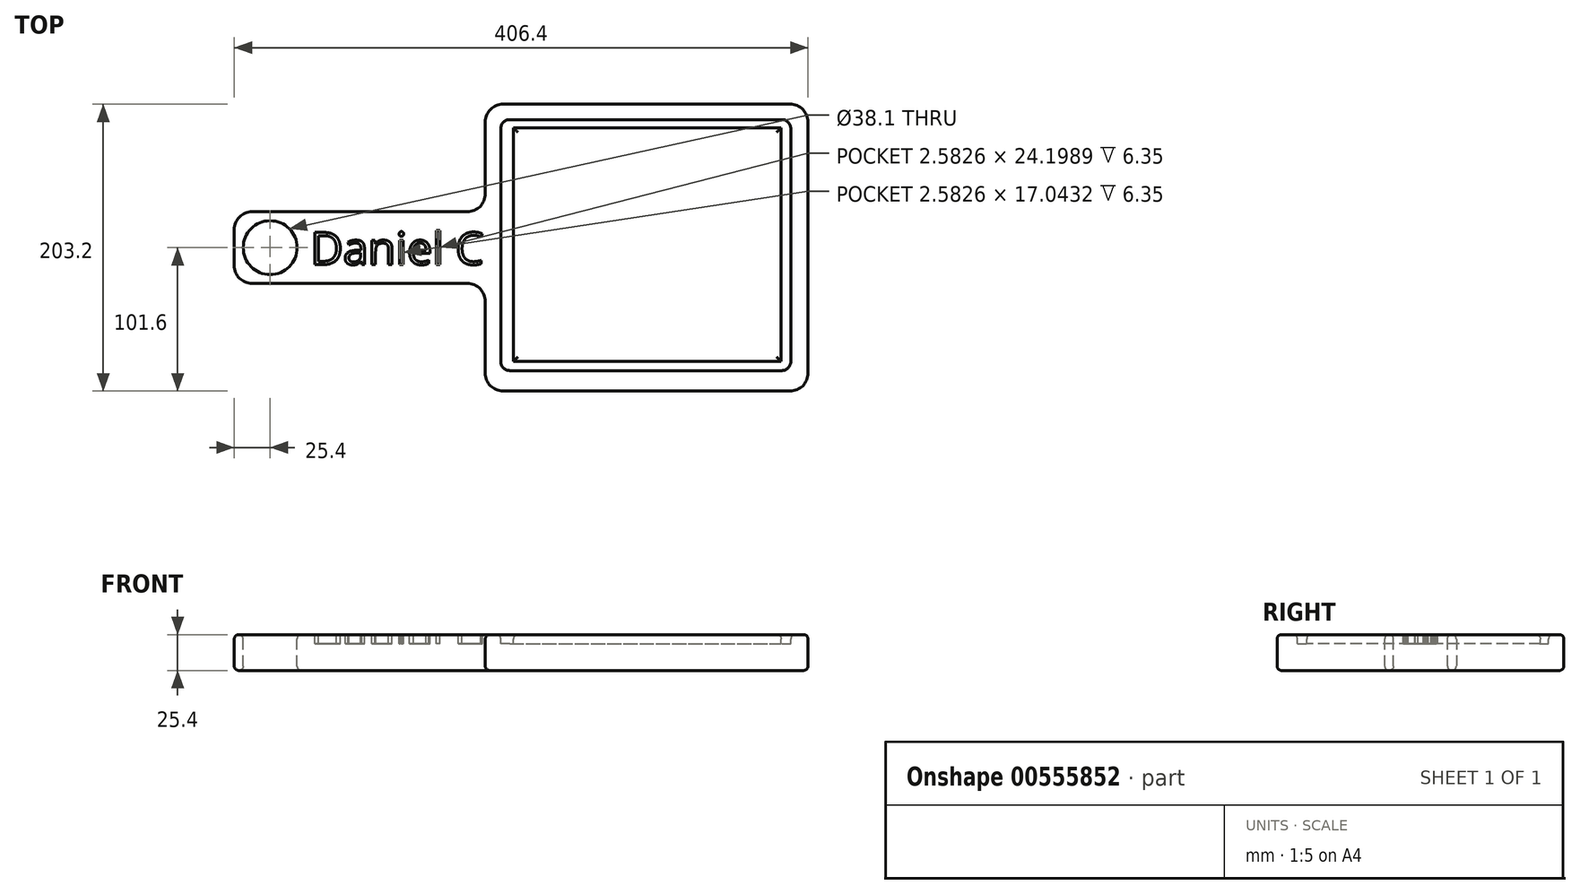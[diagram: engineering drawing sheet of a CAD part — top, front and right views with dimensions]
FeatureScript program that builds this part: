
annotation { "Feature Type Name" : "Feature", "Feature Type Description" : "" }
export const myFeature = defineFeature(function(context is Context, id is Id, definition is map)
    precondition{}
    {
        {
            var Q0;
            Q0=qCreatedBy(makeId("Top.planeOp"),FACE);
            var sketch = newSketch(context, id + "F0", { "sketchPlane" : qUnion([Q0])});
            skLineSegment(sketch, "E0.bottom", {"start": v(0, 0) * mm, "end": v(228.6, 0) * mm});
            skLineSegment(sketch, "E0.top", {"start": v(0, 203.2) * mm, "end": v(228.6, 203.2) * mm});
            skLineSegment(sketch, "E0.left", {"start": v(0, 0) * mm, "end": v(0, 203.2) * mm});
            skLineSegment(sketch, "E0.right", {"start": v(228.6, 0) * mm, "end": v(228.6, 203.2) * mm});
            skLineSegment(sketch, "E1.bottom", {"start": v(0, 127) * mm, "end": v(-177.8, 127) * mm});
            skLineSegment(sketch, "E1.top", {"start": v(0, 76.2) * mm, "end": v(-177.8, 76.2) * mm});
            skLineSegment(sketch, "E1.left", {"start": v(0, 127) * mm, "end": v(0, 76.2) * mm});
            skLineSegment(sketch, "E1.right", {"start": v(-177.8, 127) * mm, "end": v(-177.8, 76.2) * mm});
            skSolve(sketch);
        }
        {
            var Q0;
            Q0=makeQuery(id+"F0.imprint","IMPRINT",FACE,{"disambiguationData":[TD([[makeQuery(id+"F0.imprint","IMPRINT",EDGE,{"derivedFrom":sQuery(id+"F0.wireOp",EDGE,"E1.bottom")}),1.0]])]});
            var Q1;
            {var subQ3=sQuery(id+"F0.wireOp",EDGE,"E0.bottom");Q1=makeQuery(id+"F0.imprint","IMPRINT",FACE,{"disambiguationData":[TD([[makeQuery(id+"F0.imprint","IMPRINT",EDGE,{"derivedFrom":subQ3}),1.0]])]});}
            extrude(context, id + "F1", {"entities" : qUnion([Q0, Q1]), "depth" : 25.4 * mm, "offsetDistance" : 25.4 * mm});
        }
        {
            var Q0;
            Q0=makeQuery(id+"F1.opExtrude","CAP_FACE",FACE,{"disambiguationData":[OSD([sQuery(id+"F0.wireOp",EDGE,"E0.bottom"),sQuery(id+"F0.wireOp",EDGE,"E0.top"),sQuery(id+"F0.wireOp",EDGE,"E0.left"),sQuery(id+"F0.wireOp",EDGE,"E0.right"),sQuery(id+"F0.wireOp",EDGE,"E1.bottom"),sQuery(id+"F0.wireOp",EDGE,"E1.top"),sQuery(id+"F0.wireOp",EDGE,"E1.right")])],"isStart":false});
            var sketch = newSketch(context, id + "F2", { "sketchPlane" : qUnion([Q0])});
            skCircle(sketch, "E2", {"center": v(-152.4, 101.6) * mm, "radius": 19.05 * mm});
            skSolve(sketch);
        }
        {
            var Q0;
            Q0 = qSketchRegion(id + "F2", true);
            extrude(context, id + "F3", {"entities" : qUnion([Q0]), "operationType" : NewBodyOperationType.REMOVE, "oppositeDirection" : true, "depth" : 25.4 * mm, "offsetDistance" : 25.4 * mm});
        }
        {
            var Q0;
            Q0=makeQuery(id+"F1.opExtrude","CAP_FACE",FACE,{"disambiguationData":[OSD([sQuery(id+"F0.wireOp",EDGE,"E0.bottom"),sQuery(id+"F0.wireOp",EDGE,"E0.top"),sQuery(id+"F0.wireOp",EDGE,"E0.left"),sQuery(id+"F0.wireOp",EDGE,"E0.right"),sQuery(id+"F0.wireOp",EDGE,"E1.bottom"),sQuery(id+"F0.wireOp",EDGE,"E1.top"),sQuery(id+"F0.wireOp",EDGE,"E1.right")])],"isStart":false});
            var sketch = newSketch(context, id + "F4", { "sketchPlane" : qUnion([Q0])});
            skLineSegment(sketch, "E3.bottom", {"start": v(11, 192.3) * mm, "end": v(216.38, 192.3) * mm});
            skLineSegment(sketch, "E3.top", {"start": v(11, 14.5) * mm, "end": v(216.38, 14.5) * mm});
            skLineSegment(sketch, "E3.left", {"start": v(11, 192.3) * mm, "end": v(11, 14.5) * mm});
            skLineSegment(sketch, "E3.right", {"start": v(216.38, 192.3) * mm, "end": v(216.38, 14.5) * mm});
            skLineSegment(sketch, "E4.bottom", {"start": v(19.88, 186.5) * mm, "end": v(209.54, 186.5) * mm});
            skLineSegment(sketch, "E4.top", {"start": v(19.88, 20.99) * mm, "end": v(209.54, 20.99) * mm});
            skLineSegment(sketch, "E4.left", {"start": v(19.88, 186.5) * mm, "end": v(19.88, 20.99) * mm});
            skLineSegment(sketch, "E4.right", {"start": v(209.54, 186.5) * mm, "end": v(209.54, 20.99) * mm});
            skSolve(sketch);
        }
        {
            var Q0;
            Q0 = qSketchRegion(id + "F4", true);
            extrude(context, id + "F5", {"entities" : qUnion([Q0]), "operationType" : NewBodyOperationType.REMOVE, "oppositeDirection" : true, "depth" : 6.35 * mm, "offsetDistance" : 25.4 * mm});
        }
        {
            var Q0;
            Q0=makeQuery(id+"F5.boolean.opBoolean","COPY",EDGE,{"derivedFrom":makeQuery(id+"F5.opExtrude","SWEPT_EDGE",EDGE,{"disambiguationData":[OSD([sQuery(id+"F4.wireOp",EDGE,"E3.bottom"),sQuery(id+"F4.wireOp",EDGE,"E3.left")])]})});
            var Q1;
            Q1=makeQuery(id+"F5.boolean.opBoolean","COPY",EDGE,{"derivedFrom":makeQuery(id+"F5.opExtrude","SWEPT_EDGE",EDGE,{"disambiguationData":[OSD([sQuery(id+"F4.wireOp",EDGE,"E3.top"),sQuery(id+"F4.wireOp",EDGE,"E3.left")])]})});
            var Q2;
            Q2=makeQuery(id+"F5.boolean.opBoolean","COPY",EDGE,{"derivedFrom":makeQuery(id+"F5.opExtrude","SWEPT_EDGE",EDGE,{"disambiguationData":[OSD([sQuery(id+"F4.wireOp",EDGE,"E3.bottom"),sQuery(id+"F4.wireOp",EDGE,"E3.right")])]})});
            var Q3;
            Q3=makeQuery(id+"F5.boolean.opBoolean","COPY",EDGE,{"derivedFrom":makeQuery(id+"F5.opExtrude","SWEPT_EDGE",EDGE,{"disambiguationData":[OSD([sQuery(id+"F4.wireOp",EDGE,"E3.top"),sQuery(id+"F4.wireOp",EDGE,"E3.right")])]})});
            fillet(context, id + "F6", {"entities" : qUnion([Q0, Q1, Q2, Q3]), "radius" : 6.35 * mm, "tangentPropagation" : true, "allowEdgeOverflow" : false});
        }
        {
            var Q0;
            Q0=makeQuery(id+"F1.opExtrude","SWEPT_EDGE",EDGE,{"disambiguationData":[OSD([sQuery(id+"F0.wireOp",EDGE,"E0.top"),sQuery(id+"F0.wireOp",EDGE,"E0.left")])]});
            var Q1;
            Q1=makeQuery(id+"F1.opExtrude","SWEPT_EDGE",EDGE,{"disambiguationData":[OSD([sQuery(id+"F0.wireOp",EDGE,"E1.bottom"),sQuery(id+"F0.wireOp",EDGE,"E1.right")])]});
            var Q2;
            Q2=makeQuery(id+"F1.opExtrude","SWEPT_EDGE",EDGE,{"disambiguationData":[OSD([sQuery(id+"F0.wireOp",EDGE,"E1.top"),sQuery(id+"F0.wireOp",EDGE,"E1.right")])]});
            var Q3;
            Q3=makeQuery(id+"F1.opExtrude","SWEPT_EDGE",EDGE,{"disambiguationData":[OSD([sQuery(id+"F0.wireOp",EDGE,"E0.bottom"),sQuery(id+"F0.wireOp",EDGE,"E0.left")])]});
            var Q4;
            Q4=makeQuery(id+"F1.opExtrude","SWEPT_EDGE",EDGE,{"disambiguationData":[OSD([sQuery(id+"F0.wireOp",EDGE,"E0.bottom"),sQuery(id+"F0.wireOp",EDGE,"E0.right")])]});
            var Q5;
            Q5=makeQuery(id+"F1.opExtrude","SWEPT_EDGE",EDGE,{"disambiguationData":[OSD([sQuery(id+"F0.wireOp",EDGE,"E0.top"),sQuery(id+"F0.wireOp",EDGE,"E0.right")])]});
            var Q6;
            Q6=makeQuery(id+"F1.opExtrude","SWEPT_EDGE",EDGE,{"disambiguationData":[OSD([sQuery(id+"F0.wireOp",EDGE,"E0.left"),sQuery(id+"F0.wireOp",EDGE,"E1.bottom"),sQuery(id+"F0.wireOp",EDGE,"E1.left")])]});
            var Q7;
            Q7=makeQuery(id+"F1.opExtrude","SWEPT_EDGE",EDGE,{"disambiguationData":[OSD([sQuery(id+"F0.wireOp",EDGE,"E0.left"),sQuery(id+"F0.wireOp",EDGE,"E1.top"),sQuery(id+"F0.wireOp",EDGE,"E1.left")])]});
            fillet(context, id + "F7", {"entities" : qUnion([Q0, Q1, Q2, Q3, Q4, Q5, Q6, Q7]), "radius" : 12.7 * mm, "tangentPropagation" : true, "allowEdgeOverflow" : false});
        }
        {
            var Q0;
            Q0=makeQuery(id+"F5.boolean.opBoolean","SPLIT",FACE,{"disambiguationData":[TD([makeQuery(id+"F5.opExtrude","SWEPT_FACE",FACE,{"disambiguationData":[OSD([sQuery(id+"F4.wireOp",EDGE,"E4.bottom")])]})])],"derivedFrom":makeQuery(id+"F1.opExtrude","CAP_FACE",FACE,{"disambiguationData":[OSD([sQuery(id+"F0.wireOp",EDGE,"E0.bottom"),sQuery(id+"F0.wireOp",EDGE,"E0.top"),sQuery(id+"F0.wireOp",EDGE,"E0.left"),sQuery(id+"F0.wireOp",EDGE,"E0.right"),sQuery(id+"F0.wireOp",EDGE,"E1.bottom"),sQuery(id+"F0.wireOp",EDGE,"E1.top"),sQuery(id+"F0.wireOp",EDGE,"E1.right")])],"isStart":false})});
            var Q1;
            {var subQ0=sQuery(id+"F0.wireOp",EDGE,"E1.right");var subQ1=sQuery(id+"F0.wireOp",EDGE,"E1.top");var subQ2=sQuery(id+"F0.wireOp",EDGE,"E1.bottom");var subQ3=sQuery(id+"F0.wireOp",EDGE,"E0.right");var subQ4=sQuery(id+"F0.wireOp",EDGE,"E0.bottom");var subQ5=sQuery(id+"F0.wireOp",EDGE,"E0.left");var subQ6=sQuery(id+"F0.wireOp",EDGE,"E0.top");Q1=makeQuery(id+"F5.boolean.opBoolean","SPLIT",FACE,{"disambiguationData":[TD([makeQuery(id+"F1.opExtrude","SWEPT_FACE",FACE,{"disambiguationData":[OSD([subQ4])]})])],"derivedFrom":makeQuery(id+"F1.opExtrude","CAP_FACE",FACE,{"disambiguationData":[OSD([subQ4,subQ6,subQ5,subQ3,subQ2,subQ1,subQ0])],"isStart":false})});}
            var Q2;
            Q2=makeQuery(id+"F1.opExtrude","CAP_FACE",FACE,{"disambiguationData":[OSD([sQuery(id+"F0.wireOp",EDGE,"E0.bottom"),sQuery(id+"F0.wireOp",EDGE,"E0.top"),sQuery(id+"F0.wireOp",EDGE,"E0.left"),sQuery(id+"F0.wireOp",EDGE,"E0.right"),sQuery(id+"F0.wireOp",EDGE,"E1.bottom"),sQuery(id+"F0.wireOp",EDGE,"E1.top"),sQuery(id+"F0.wireOp",EDGE,"E1.right")])],"isStart":true});
            fillet(context, id + "F8", {"entities" : qUnion([Q0, Q1, Q2]), "radius" : 3.17 * mm, "tangentPropagation" : true, "allowEdgeOverflow" : false});
        }
        {
            var Q0;
            {var subQ0=sQuery(id+"F0.wireOp",EDGE,"E1.right");var subQ1=sQuery(id+"F0.wireOp",EDGE,"E1.top");var subQ2=sQuery(id+"F0.wireOp",EDGE,"E1.bottom");var subQ3=sQuery(id+"F0.wireOp",EDGE,"E0.right");var subQ4=sQuery(id+"F0.wireOp",EDGE,"E0.bottom");var subQ5=sQuery(id+"F0.wireOp",EDGE,"E0.left");var subQ6=sQuery(id+"F0.wireOp",EDGE,"E0.top");Q0=makeQuery(id+"F8.opFillet","SPLIT",FACE,{"disambiguationData":[OD(0.0)],"derivedFrom":makeQuery(id+"F5.boolean.opBoolean","SPLIT",FACE,{"disambiguationData":[TD([makeQuery(id+"F1.opExtrude","SWEPT_FACE",FACE,{"disambiguationData":[OSD([subQ4])]})])],"derivedFrom":makeQuery(id+"F1.opExtrude","CAP_FACE",FACE,{"disambiguationData":[OSD([subQ4,subQ6,subQ5,subQ3,subQ2,subQ1,subQ0])],"isStart":false})})});}
            var sketch = newSketch(context, id + "F9", { "sketchPlane" : qUnion([Q0])});
            skText(sketch, "E5", { "text": "Daniel C", "fontName": "OpenSans-Regular.ttf"});
            const initialGuessF9  = {"E5": [-0.12396, 0.08963, 1, 0, 0.02293]};
            skSetInitialGuess(sketch, initialGuessF9);
            skSolve(sketch);
        }
        {
            var Q0;
            Q0 = qSketchRegion(id + "F9", true);
            extrude(context, id + "F10", {"entities" : qUnion([Q0]), "operationType" : NewBodyOperationType.REMOVE, "oppositeDirection" : true, "depth" : 6.35 * mm, "offsetDistance" : 25.4 * mm});
        }
    });
